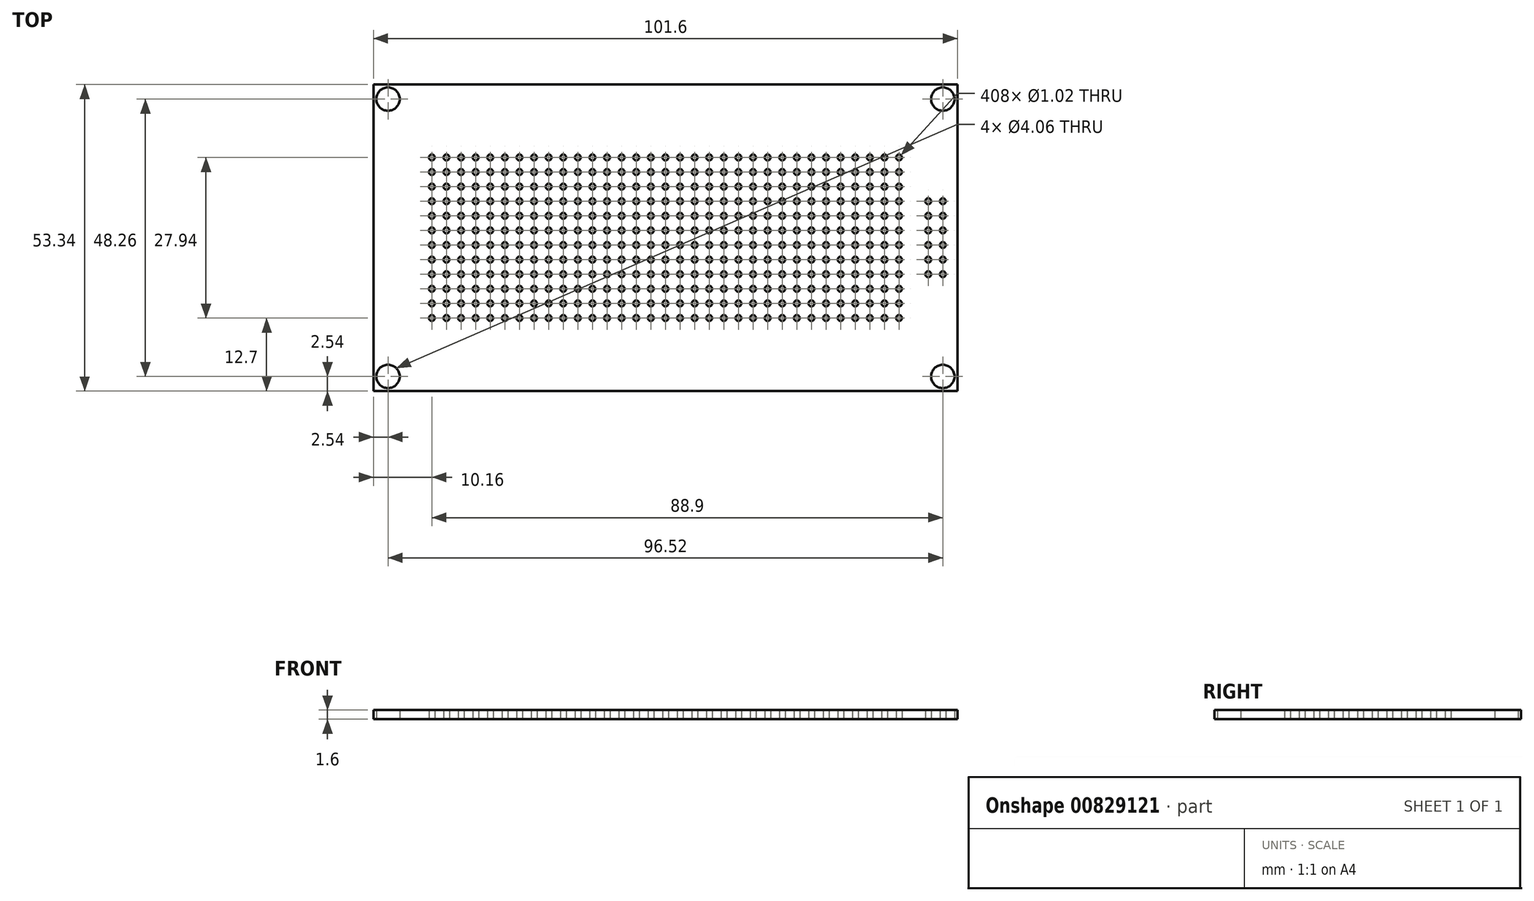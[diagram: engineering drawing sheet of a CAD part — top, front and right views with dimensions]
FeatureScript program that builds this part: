
annotation { "Feature Type Name" : "Feature", "Feature Type Description" : "" }
export const myFeature = defineFeature(function(context is Context, id is Id, definition is map)
    precondition{}
    {
        {
            var Q0;
            Q0=qCreatedBy(makeId("Top.planeOp"),FACE);
            var sketch = newSketch(context, id + "F0", { "sketchPlane" : qUnion([Q0])});
            skLineSegment(sketch, "E0.bottom", {"start": v(50.8, -26.67) * mm, "end": v(-50.8, -26.67) * mm});
            skLineSegment(sketch, "E0.top", {"start": v(50.8, 26.67) * mm, "end": v(-50.8, 26.67) * mm});
            skLineSegment(sketch, "E0.left", {"start": v(50.8, -26.67) * mm, "end": v(50.8, 26.67) * mm});
            skLineSegment(sketch, "E0.right", {"start": v(-50.8, -26.67) * mm, "end": v(-50.8, 26.67) * mm});
            skPoint(sketch, "E0.middle", {"position": v(0, 0) * mm});
            skCircle(sketch, "E1", {"center": v(-48.26, -24.13) * mm, "radius": 2.03 * mm});
            skCircle(sketch, "E2", {"center": v(-48.26, 24.13) * mm, "radius": 2.03 * mm});
            skCircle(sketch, "E3", {"center": v(48.26, 24.13) * mm, "radius": 2.03 * mm});
            skCircle(sketch, "E4", {"center": v(48.26, -24.13) * mm, "radius": 2.03 * mm});
            skCircle(sketch, "E5", {"center": v(-40.64, -13.97) * mm, "radius": 0.5 * mm});
            skCircle(sketch, "E6.0.1.0", {"center": v(-40.64, -11.43) * mm, "radius": 0.5 * mm});
            skCircle(sketch, "E6.0.2.0", {"center": v(-40.64, -8.9) * mm, "radius": 0.5 * mm});
            skCircle(sketch, "E6.0.3.0", {"center": v(-40.64, -6.35) * mm, "radius": 0.5 * mm});
            skCircle(sketch, "E6.0.4.0", {"center": v(-40.64, -3.81) * mm, "radius": 0.5 * mm});
            skCircle(sketch, "E6.0.5.0", {"center": v(-40.64, -1.27) * mm, "radius": 0.5 * mm});
            skCircle(sketch, "E6.0.6.0", {"center": v(-40.64, 1.27) * mm, "radius": 0.5 * mm});
            skCircle(sketch, "E6.0.7.0", {"center": v(-40.64, 3.8) * mm, "radius": 0.5 * mm});
            skCircle(sketch, "E6.0.8.0", {"center": v(-40.64, 6.35) * mm, "radius": 0.5 * mm});
            skCircle(sketch, "E6.0.9.0", {"center": v(-40.64, 8.89) * mm, "radius": 0.5 * mm});
            skCircle(sketch, "E6.0.10.0", {"center": v(-40.64, 11.43) * mm, "radius": 0.5 * mm});
            skCircle(sketch, "E6.0.11.0", {"center": v(-40.64, 13.97) * mm, "radius": 0.5 * mm});
            skCircle(sketch, "E6.1.0.0", {"center": v(-38.1, -13.97) * mm, "radius": 0.5 * mm});
            skCircle(sketch, "E6.1.1.0", {"center": v(-38.1, -11.43) * mm, "radius": 0.5 * mm});
            skCircle(sketch, "E6.1.2.0", {"center": v(-38.1, -8.9) * mm, "radius": 0.5 * mm});
            skCircle(sketch, "E6.1.3.0", {"center": v(-38.1, -6.35) * mm, "radius": 0.5 * mm});
            skCircle(sketch, "E6.1.4.0", {"center": v(-38.1, -3.81) * mm, "radius": 0.5 * mm});
            skCircle(sketch, "E6.1.5.0", {"center": v(-38.1, -1.27) * mm, "radius": 0.5 * mm});
            skCircle(sketch, "E6.1.6.0", {"center": v(-38.1, 1.27) * mm, "radius": 0.5 * mm});
            skCircle(sketch, "E6.1.7.0", {"center": v(-38.1, 3.8) * mm, "radius": 0.5 * mm});
            skCircle(sketch, "E6.1.8.0", {"center": v(-38.1, 6.35) * mm, "radius": 0.5 * mm});
            skCircle(sketch, "E6.1.9.0", {"center": v(-38.1, 8.89) * mm, "radius": 0.5 * mm});
            skCircle(sketch, "E6.1.10.0", {"center": v(-38.1, 11.43) * mm, "radius": 0.5 * mm});
            skCircle(sketch, "E6.1.11.0", {"center": v(-38.1, 13.97) * mm, "radius": 0.5 * mm});
            skCircle(sketch, "E6.2.0.0", {"center": v(-35.56, -13.97) * mm, "radius": 0.5 * mm});
            skCircle(sketch, "E6.2.1.0", {"center": v(-35.56, -11.43) * mm, "radius": 0.5 * mm});
            skCircle(sketch, "E6.2.2.0", {"center": v(-35.56, -8.9) * mm, "radius": 0.5 * mm});
            skCircle(sketch, "E6.2.3.0", {"center": v(-35.56, -6.35) * mm, "radius": 0.5 * mm});
            skCircle(sketch, "E6.2.4.0", {"center": v(-35.56, -3.81) * mm, "radius": 0.5 * mm});
            skCircle(sketch, "E6.2.5.0", {"center": v(-35.56, -1.27) * mm, "radius": 0.5 * mm});
            skCircle(sketch, "E6.2.6.0", {"center": v(-35.56, 1.27) * mm, "radius": 0.5 * mm});
            skCircle(sketch, "E6.2.7.0", {"center": v(-35.56, 3.8) * mm, "radius": 0.5 * mm});
            skCircle(sketch, "E6.2.8.0", {"center": v(-35.56, 6.35) * mm, "radius": 0.5 * mm});
            skCircle(sketch, "E6.2.9.0", {"center": v(-35.56, 8.89) * mm, "radius": 0.5 * mm});
            skCircle(sketch, "E6.2.10.0", {"center": v(-35.56, 11.43) * mm, "radius": 0.5 * mm});
            skCircle(sketch, "E6.2.11.0", {"center": v(-35.56, 13.97) * mm, "radius": 0.5 * mm});
            skCircle(sketch, "E6.3.0.0", {"center": v(-33.02, -13.97) * mm, "radius": 0.5 * mm});
            skCircle(sketch, "E6.3.1.0", {"center": v(-33.02, -11.43) * mm, "radius": 0.5 * mm});
            skCircle(sketch, "E6.3.2.0", {"center": v(-33.02, -8.9) * mm, "radius": 0.5 * mm});
            skCircle(sketch, "E6.3.3.0", {"center": v(-33.02, -6.35) * mm, "radius": 0.5 * mm});
            skCircle(sketch, "E6.3.4.0", {"center": v(-33.02, -3.81) * mm, "radius": 0.5 * mm});
            skCircle(sketch, "E6.3.5.0", {"center": v(-33.02, -1.27) * mm, "radius": 0.5 * mm});
            skCircle(sketch, "E6.3.6.0", {"center": v(-33.02, 1.27) * mm, "radius": 0.5 * mm});
            skCircle(sketch, "E6.3.7.0", {"center": v(-33.02, 3.8) * mm, "radius": 0.5 * mm});
            skCircle(sketch, "E6.3.8.0", {"center": v(-33.02, 6.35) * mm, "radius": 0.5 * mm});
            skCircle(sketch, "E6.3.9.0", {"center": v(-33.02, 8.89) * mm, "radius": 0.5 * mm});
            skCircle(sketch, "E6.3.10.0", {"center": v(-33.02, 11.43) * mm, "radius": 0.5 * mm});
            skCircle(sketch, "E6.3.11.0", {"center": v(-33.02, 13.97) * mm, "radius": 0.5 * mm});
            skCircle(sketch, "E6.4.0.0", {"center": v(-30.48, -13.97) * mm, "radius": 0.5 * mm});
            skCircle(sketch, "E6.4.1.0", {"center": v(-30.48, -11.43) * mm, "radius": 0.5 * mm});
            skCircle(sketch, "E6.4.2.0", {"center": v(-30.48, -8.9) * mm, "radius": 0.5 * mm});
            skCircle(sketch, "E6.4.3.0", {"center": v(-30.48, -6.35) * mm, "radius": 0.5 * mm});
            skCircle(sketch, "E6.4.4.0", {"center": v(-30.48, -3.81) * mm, "radius": 0.5 * mm});
            skCircle(sketch, "E6.4.5.0", {"center": v(-30.48, -1.27) * mm, "radius": 0.5 * mm});
            skCircle(sketch, "E6.4.6.0", {"center": v(-30.48, 1.27) * mm, "radius": 0.5 * mm});
            skCircle(sketch, "E6.4.7.0", {"center": v(-30.48, 3.8) * mm, "radius": 0.5 * mm});
            skCircle(sketch, "E6.4.8.0", {"center": v(-30.48, 6.35) * mm, "radius": 0.5 * mm});
            skCircle(sketch, "E6.4.9.0", {"center": v(-30.48, 8.89) * mm, "radius": 0.5 * mm});
            skCircle(sketch, "E6.4.10.0", {"center": v(-30.48, 11.43) * mm, "radius": 0.5 * mm});
            skCircle(sketch, "E6.4.11.0", {"center": v(-30.48, 13.97) * mm, "radius": 0.5 * mm});
            skCircle(sketch, "E6.5.0.0", {"center": v(-27.94, -13.97) * mm, "radius": 0.5 * mm});
            skCircle(sketch, "E6.5.1.0", {"center": v(-27.94, -11.43) * mm, "radius": 0.5 * mm});
            skCircle(sketch, "E6.5.2.0", {"center": v(-27.94, -8.9) * mm, "radius": 0.5 * mm});
            skCircle(sketch, "E6.5.3.0", {"center": v(-27.94, -6.35) * mm, "radius": 0.5 * mm});
            skCircle(sketch, "E6.5.4.0", {"center": v(-27.94, -3.81) * mm, "radius": 0.5 * mm});
            skCircle(sketch, "E6.5.5.0", {"center": v(-27.94, -1.27) * mm, "radius": 0.5 * mm});
            skCircle(sketch, "E6.5.6.0", {"center": v(-27.94, 1.27) * mm, "radius": 0.5 * mm});
            skCircle(sketch, "E6.5.7.0", {"center": v(-27.94, 3.8) * mm, "radius": 0.5 * mm});
            skCircle(sketch, "E6.5.8.0", {"center": v(-27.94, 6.35) * mm, "radius": 0.5 * mm});
            skCircle(sketch, "E6.5.9.0", {"center": v(-27.94, 8.89) * mm, "radius": 0.5 * mm});
            skCircle(sketch, "E6.5.10.0", {"center": v(-27.94, 11.43) * mm, "radius": 0.5 * mm});
            skCircle(sketch, "E6.5.11.0", {"center": v(-27.94, 13.97) * mm, "radius": 0.5 * mm});
            skCircle(sketch, "E6.6.0.0", {"center": v(-25.4, -13.97) * mm, "radius": 0.5 * mm});
            skCircle(sketch, "E6.6.1.0", {"center": v(-25.4, -11.43) * mm, "radius": 0.5 * mm});
            skCircle(sketch, "E6.6.2.0", {"center": v(-25.4, -8.9) * mm, "radius": 0.5 * mm});
            skCircle(sketch, "E6.6.3.0", {"center": v(-25.4, -6.35) * mm, "radius": 0.5 * mm});
            skCircle(sketch, "E6.6.4.0", {"center": v(-25.4, -3.81) * mm, "radius": 0.5 * mm});
            skCircle(sketch, "E6.6.5.0", {"center": v(-25.4, -1.27) * mm, "radius": 0.5 * mm});
            skCircle(sketch, "E6.6.6.0", {"center": v(-25.4, 1.27) * mm, "radius": 0.5 * mm});
            skCircle(sketch, "E6.6.7.0", {"center": v(-25.4, 3.8) * mm, "radius": 0.5 * mm});
            skCircle(sketch, "E6.6.8.0", {"center": v(-25.4, 6.35) * mm, "radius": 0.5 * mm});
            skCircle(sketch, "E6.6.9.0", {"center": v(-25.4, 8.89) * mm, "radius": 0.5 * mm});
            skCircle(sketch, "E6.6.10.0", {"center": v(-25.4, 11.43) * mm, "radius": 0.5 * mm});
            skCircle(sketch, "E6.6.11.0", {"center": v(-25.4, 13.97) * mm, "radius": 0.5 * mm});
            skCircle(sketch, "E6.7.0.0", {"center": v(-22.86, -13.97) * mm, "radius": 0.5 * mm});
            skCircle(sketch, "E6.7.1.0", {"center": v(-22.86, -11.43) * mm, "radius": 0.5 * mm});
            skCircle(sketch, "E6.7.2.0", {"center": v(-22.86, -8.9) * mm, "radius": 0.5 * mm});
            skCircle(sketch, "E6.7.3.0", {"center": v(-22.86, -6.35) * mm, "radius": 0.5 * mm});
            skCircle(sketch, "E6.7.4.0", {"center": v(-22.86, -3.81) * mm, "radius": 0.5 * mm});
            skCircle(sketch, "E6.7.5.0", {"center": v(-22.86, -1.27) * mm, "radius": 0.5 * mm});
            skCircle(sketch, "E6.7.6.0", {"center": v(-22.86, 1.27) * mm, "radius": 0.5 * mm});
            skCircle(sketch, "E6.7.7.0", {"center": v(-22.86, 3.8) * mm, "radius": 0.5 * mm});
            skCircle(sketch, "E6.7.8.0", {"center": v(-22.86, 6.35) * mm, "radius": 0.5 * mm});
            skCircle(sketch, "E6.7.9.0", {"center": v(-22.86, 8.89) * mm, "radius": 0.5 * mm});
            skCircle(sketch, "E6.7.10.0", {"center": v(-22.86, 11.43) * mm, "radius": 0.5 * mm});
            skCircle(sketch, "E6.7.11.0", {"center": v(-22.86, 13.97) * mm, "radius": 0.5 * mm});
            skCircle(sketch, "E6.8.0.0", {"center": v(-20.32, -13.97) * mm, "radius": 0.5 * mm});
            skCircle(sketch, "E6.8.1.0", {"center": v(-20.32, -11.43) * mm, "radius": 0.5 * mm});
            skCircle(sketch, "E6.8.2.0", {"center": v(-20.32, -8.9) * mm, "radius": 0.5 * mm});
            skCircle(sketch, "E6.8.3.0", {"center": v(-20.32, -6.35) * mm, "radius": 0.5 * mm});
            skCircle(sketch, "E6.8.4.0", {"center": v(-20.32, -3.81) * mm, "radius": 0.5 * mm});
            skCircle(sketch, "E6.8.5.0", {"center": v(-20.32, -1.27) * mm, "radius": 0.5 * mm});
            skCircle(sketch, "E6.8.6.0", {"center": v(-20.32, 1.27) * mm, "radius": 0.5 * mm});
            skCircle(sketch, "E6.8.7.0", {"center": v(-20.32, 3.8) * mm, "radius": 0.5 * mm});
            skCircle(sketch, "E6.8.8.0", {"center": v(-20.32, 6.35) * mm, "radius": 0.5 * mm});
            skCircle(sketch, "E6.8.9.0", {"center": v(-20.32, 8.89) * mm, "radius": 0.5 * mm});
            skCircle(sketch, "E6.8.10.0", {"center": v(-20.32, 11.43) * mm, "radius": 0.5 * mm});
            skCircle(sketch, "E6.8.11.0", {"center": v(-20.32, 13.97) * mm, "radius": 0.5 * mm});
            skCircle(sketch, "E6.9.0.0", {"center": v(-17.78, -13.97) * mm, "radius": 0.5 * mm});
            skCircle(sketch, "E6.9.1.0", {"center": v(-17.78, -11.43) * mm, "radius": 0.5 * mm});
            skCircle(sketch, "E6.9.2.0", {"center": v(-17.78, -8.9) * mm, "radius": 0.5 * mm});
            skCircle(sketch, "E6.9.3.0", {"center": v(-17.78, -6.35) * mm, "radius": 0.5 * mm});
            skCircle(sketch, "E6.9.4.0", {"center": v(-17.78, -3.81) * mm, "radius": 0.5 * mm});
            skCircle(sketch, "E6.9.5.0", {"center": v(-17.78, -1.27) * mm, "radius": 0.5 * mm});
            skCircle(sketch, "E6.9.6.0", {"center": v(-17.78, 1.27) * mm, "radius": 0.5 * mm});
            skCircle(sketch, "E6.9.7.0", {"center": v(-17.78, 3.8) * mm, "radius": 0.5 * mm});
            skCircle(sketch, "E6.9.8.0", {"center": v(-17.78, 6.35) * mm, "radius": 0.5 * mm});
            skCircle(sketch, "E6.9.9.0", {"center": v(-17.78, 8.89) * mm, "radius": 0.5 * mm});
            skCircle(sketch, "E6.9.10.0", {"center": v(-17.78, 11.43) * mm, "radius": 0.5 * mm});
            skCircle(sketch, "E6.9.11.0", {"center": v(-17.78, 13.97) * mm, "radius": 0.5 * mm});
            skCircle(sketch, "E6.10.0.0", {"center": v(-15.24, -13.97) * mm, "radius": 0.5 * mm});
            skCircle(sketch, "E6.10.1.0", {"center": v(-15.24, -11.43) * mm, "radius": 0.5 * mm});
            skCircle(sketch, "E6.10.2.0", {"center": v(-15.24, -8.9) * mm, "radius": 0.5 * mm});
            skCircle(sketch, "E6.10.3.0", {"center": v(-15.24, -6.35) * mm, "radius": 0.5 * mm});
            skCircle(sketch, "E6.10.4.0", {"center": v(-15.24, -3.81) * mm, "radius": 0.5 * mm});
            skCircle(sketch, "E6.10.5.0", {"center": v(-15.24, -1.27) * mm, "radius": 0.5 * mm});
            skCircle(sketch, "E6.10.6.0", {"center": v(-15.24, 1.27) * mm, "radius": 0.5 * mm});
            skCircle(sketch, "E6.10.7.0", {"center": v(-15.24, 3.8) * mm, "radius": 0.5 * mm});
            skCircle(sketch, "E6.10.8.0", {"center": v(-15.24, 6.35) * mm, "radius": 0.5 * mm});
            skCircle(sketch, "E6.10.9.0", {"center": v(-15.24, 8.89) * mm, "radius": 0.5 * mm});
            skCircle(sketch, "E6.10.10.0", {"center": v(-15.24, 11.43) * mm, "radius": 0.5 * mm});
            skCircle(sketch, "E6.10.11.0", {"center": v(-15.24, 13.97) * mm, "radius": 0.5 * mm});
            skCircle(sketch, "E6.11.0.0", {"center": v(-12.7, -13.97) * mm, "radius": 0.5 * mm});
            skCircle(sketch, "E6.11.1.0", {"center": v(-12.7, -11.43) * mm, "radius": 0.5 * mm});
            skCircle(sketch, "E6.11.2.0", {"center": v(-12.7, -8.9) * mm, "radius": 0.5 * mm});
            skCircle(sketch, "E6.11.3.0", {"center": v(-12.7, -6.35) * mm, "radius": 0.5 * mm});
            skCircle(sketch, "E6.11.4.0", {"center": v(-12.7, -3.81) * mm, "radius": 0.5 * mm});
            skCircle(sketch, "E6.11.5.0", {"center": v(-12.7, -1.27) * mm, "radius": 0.5 * mm});
            skCircle(sketch, "E6.11.6.0", {"center": v(-12.7, 1.27) * mm, "radius": 0.5 * mm});
            skCircle(sketch, "E6.11.7.0", {"center": v(-12.7, 3.8) * mm, "radius": 0.5 * mm});
            skCircle(sketch, "E6.11.8.0", {"center": v(-12.7, 6.35) * mm, "radius": 0.5 * mm});
            skCircle(sketch, "E6.11.9.0", {"center": v(-12.7, 8.89) * mm, "radius": 0.5 * mm});
            skCircle(sketch, "E6.11.10.0", {"center": v(-12.7, 11.43) * mm, "radius": 0.5 * mm});
            skCircle(sketch, "E6.11.11.0", {"center": v(-12.7, 13.97) * mm, "radius": 0.5 * mm});
            skCircle(sketch, "E6.12.0.0", {"center": v(-10.16, -13.97) * mm, "radius": 0.5 * mm});
            skCircle(sketch, "E6.12.1.0", {"center": v(-10.16, -11.43) * mm, "radius": 0.5 * mm});
            skCircle(sketch, "E6.12.2.0", {"center": v(-10.16, -8.9) * mm, "radius": 0.5 * mm});
            skCircle(sketch, "E6.12.3.0", {"center": v(-10.16, -6.35) * mm, "radius": 0.5 * mm});
            skCircle(sketch, "E6.12.4.0", {"center": v(-10.16, -3.81) * mm, "radius": 0.5 * mm});
            skCircle(sketch, "E6.12.5.0", {"center": v(-10.16, -1.27) * mm, "radius": 0.5 * mm});
            skCircle(sketch, "E6.12.6.0", {"center": v(-10.16, 1.27) * mm, "radius": 0.5 * mm});
            skCircle(sketch, "E6.12.7.0", {"center": v(-10.16, 3.8) * mm, "radius": 0.5 * mm});
            skCircle(sketch, "E6.12.8.0", {"center": v(-10.16, 6.35) * mm, "radius": 0.5 * mm});
            skCircle(sketch, "E6.12.9.0", {"center": v(-10.16, 8.89) * mm, "radius": 0.5 * mm});
            skCircle(sketch, "E6.12.10.0", {"center": v(-10.16, 11.43) * mm, "radius": 0.5 * mm});
            skCircle(sketch, "E6.12.11.0", {"center": v(-10.16, 13.97) * mm, "radius": 0.5 * mm});
            skCircle(sketch, "E6.13.0.0", {"center": v(-7.62, -13.97) * mm, "radius": 0.5 * mm});
            skCircle(sketch, "E6.13.1.0", {"center": v(-7.62, -11.43) * mm, "radius": 0.5 * mm});
            skCircle(sketch, "E6.13.2.0", {"center": v(-7.62, -8.9) * mm, "radius": 0.5 * mm});
            skCircle(sketch, "E6.13.3.0", {"center": v(-7.62, -6.35) * mm, "radius": 0.5 * mm});
            skCircle(sketch, "E6.13.4.0", {"center": v(-7.62, -3.81) * mm, "radius": 0.5 * mm});
            skCircle(sketch, "E6.13.5.0", {"center": v(-7.62, -1.27) * mm, "radius": 0.5 * mm});
            skCircle(sketch, "E6.13.6.0", {"center": v(-7.62, 1.27) * mm, "radius": 0.5 * mm});
            skCircle(sketch, "E6.13.7.0", {"center": v(-7.62, 3.8) * mm, "radius": 0.5 * mm});
            skCircle(sketch, "E6.13.8.0", {"center": v(-7.62, 6.35) * mm, "radius": 0.5 * mm});
            skCircle(sketch, "E6.13.9.0", {"center": v(-7.62, 8.89) * mm, "radius": 0.5 * mm});
            skCircle(sketch, "E6.13.10.0", {"center": v(-7.62, 11.43) * mm, "radius": 0.5 * mm});
            skCircle(sketch, "E6.13.11.0", {"center": v(-7.62, 13.97) * mm, "radius": 0.5 * mm});
            skCircle(sketch, "E6.14.0.0", {"center": v(-5.08, -13.97) * mm, "radius": 0.5 * mm});
            skCircle(sketch, "E6.14.1.0", {"center": v(-5.08, -11.43) * mm, "radius": 0.5 * mm});
            skCircle(sketch, "E6.14.2.0", {"center": v(-5.08, -8.9) * mm, "radius": 0.5 * mm});
            skCircle(sketch, "E6.14.3.0", {"center": v(-5.08, -6.35) * mm, "radius": 0.5 * mm});
            skCircle(sketch, "E6.14.4.0", {"center": v(-5.08, -3.81) * mm, "radius": 0.5 * mm});
            skCircle(sketch, "E6.14.5.0", {"center": v(-5.08, -1.27) * mm, "radius": 0.5 * mm});
            skCircle(sketch, "E6.14.6.0", {"center": v(-5.08, 1.27) * mm, "radius": 0.5 * mm});
            skCircle(sketch, "E6.14.7.0", {"center": v(-5.08, 3.8) * mm, "radius": 0.5 * mm});
            skCircle(sketch, "E6.14.8.0", {"center": v(-5.08, 6.35) * mm, "radius": 0.5 * mm});
            skCircle(sketch, "E6.14.9.0", {"center": v(-5.08, 8.89) * mm, "radius": 0.5 * mm});
            skCircle(sketch, "E6.14.10.0", {"center": v(-5.08, 11.43) * mm, "radius": 0.5 * mm});
            skCircle(sketch, "E6.14.11.0", {"center": v(-5.08, 13.97) * mm, "radius": 0.5 * mm});
            skCircle(sketch, "E6.15.0.0", {"center": v(-2.54, -13.97) * mm, "radius": 0.5 * mm});
            skCircle(sketch, "E6.15.1.0", {"center": v(-2.54, -11.43) * mm, "radius": 0.5 * mm});
            skCircle(sketch, "E6.15.2.0", {"center": v(-2.54, -8.9) * mm, "radius": 0.5 * mm});
            skCircle(sketch, "E6.15.3.0", {"center": v(-2.54, -6.35) * mm, "radius": 0.5 * mm});
            skCircle(sketch, "E6.15.4.0", {"center": v(-2.54, -3.81) * mm, "radius": 0.5 * mm});
            skCircle(sketch, "E6.15.5.0", {"center": v(-2.54, -1.27) * mm, "radius": 0.5 * mm});
            skCircle(sketch, "E6.15.6.0", {"center": v(-2.54, 1.27) * mm, "radius": 0.5 * mm});
            skCircle(sketch, "E6.15.7.0", {"center": v(-2.54, 3.8) * mm, "radius": 0.5 * mm});
            skCircle(sketch, "E6.15.8.0", {"center": v(-2.54, 6.35) * mm, "radius": 0.5 * mm});
            skCircle(sketch, "E6.15.9.0", {"center": v(-2.54, 8.89) * mm, "radius": 0.5 * mm});
            skCircle(sketch, "E6.15.10.0", {"center": v(-2.54, 11.43) * mm, "radius": 0.5 * mm});
            skCircle(sketch, "E6.15.11.0", {"center": v(-2.54, 13.97) * mm, "radius": 0.5 * mm});
            skCircle(sketch, "E6.16.0.0", {"center": v(0, -13.97) * mm, "radius": 0.5 * mm});
            skCircle(sketch, "E6.16.1.0", {"center": v(0, -11.43) * mm, "radius": 0.5 * mm});
            skCircle(sketch, "E6.16.2.0", {"center": v(0, -8.9) * mm, "radius": 0.5 * mm});
            skCircle(sketch, "E6.16.3.0", {"center": v(0, -6.35) * mm, "radius": 0.5 * mm});
            skCircle(sketch, "E6.16.4.0", {"center": v(0, -3.81) * mm, "radius": 0.5 * mm});
            skCircle(sketch, "E6.16.5.0", {"center": v(0, -1.27) * mm, "radius": 0.5 * mm});
            skCircle(sketch, "E6.16.6.0", {"center": v(0, 1.27) * mm, "radius": 0.5 * mm});
            skCircle(sketch, "E6.16.7.0", {"center": v(0, 3.8) * mm, "radius": 0.5 * mm});
            skCircle(sketch, "E6.16.8.0", {"center": v(0, 6.35) * mm, "radius": 0.5 * mm});
            skCircle(sketch, "E6.16.9.0", {"center": v(0, 8.89) * mm, "radius": 0.5 * mm});
            skCircle(sketch, "E6.16.10.0", {"center": v(0, 11.43) * mm, "radius": 0.5 * mm});
            skCircle(sketch, "E6.16.11.0", {"center": v(0, 13.97) * mm, "radius": 0.5 * mm});
            skCircle(sketch, "E6.17.0.0", {"center": v(2.54, -13.97) * mm, "radius": 0.5 * mm});
            skCircle(sketch, "E6.17.1.0", {"center": v(2.54, -11.43) * mm, "radius": 0.5 * mm});
            skCircle(sketch, "E6.17.2.0", {"center": v(2.54, -8.9) * mm, "radius": 0.5 * mm});
            skCircle(sketch, "E6.17.3.0", {"center": v(2.54, -6.35) * mm, "radius": 0.5 * mm});
            skCircle(sketch, "E6.17.4.0", {"center": v(2.54, -3.81) * mm, "radius": 0.5 * mm});
            skCircle(sketch, "E6.17.5.0", {"center": v(2.54, -1.27) * mm, "radius": 0.5 * mm});
            skCircle(sketch, "E6.17.6.0", {"center": v(2.54, 1.27) * mm, "radius": 0.5 * mm});
            skCircle(sketch, "E6.17.7.0", {"center": v(2.54, 3.8) * mm, "radius": 0.5 * mm});
            skCircle(sketch, "E6.17.8.0", {"center": v(2.54, 6.35) * mm, "radius": 0.5 * mm});
            skCircle(sketch, "E6.17.9.0", {"center": v(2.54, 8.89) * mm, "radius": 0.5 * mm});
            skCircle(sketch, "E6.17.10.0", {"center": v(2.54, 11.43) * mm, "radius": 0.5 * mm});
            skCircle(sketch, "E6.17.11.0", {"center": v(2.54, 13.97) * mm, "radius": 0.5 * mm});
            skCircle(sketch, "E6.18.0.0", {"center": v(5.08, -13.97) * mm, "radius": 0.5 * mm});
            skCircle(sketch, "E6.18.1.0", {"center": v(5.08, -11.43) * mm, "radius": 0.5 * mm});
            skCircle(sketch, "E6.18.2.0", {"center": v(5.08, -8.9) * mm, "radius": 0.5 * mm});
            skCircle(sketch, "E6.18.3.0", {"center": v(5.08, -6.35) * mm, "radius": 0.5 * mm});
            skCircle(sketch, "E6.18.4.0", {"center": v(5.08, -3.81) * mm, "radius": 0.5 * mm});
            skCircle(sketch, "E6.18.5.0", {"center": v(5.08, -1.27) * mm, "radius": 0.5 * mm});
            skCircle(sketch, "E6.18.6.0", {"center": v(5.08, 1.27) * mm, "radius": 0.5 * mm});
            skCircle(sketch, "E6.18.7.0", {"center": v(5.08, 3.8) * mm, "radius": 0.5 * mm});
            skCircle(sketch, "E6.18.8.0", {"center": v(5.08, 6.35) * mm, "radius": 0.5 * mm});
            skCircle(sketch, "E6.18.9.0", {"center": v(5.08, 8.89) * mm, "radius": 0.5 * mm});
            skCircle(sketch, "E6.18.10.0", {"center": v(5.08, 11.43) * mm, "radius": 0.5 * mm});
            skCircle(sketch, "E6.18.11.0", {"center": v(5.08, 13.97) * mm, "radius": 0.5 * mm});
            skCircle(sketch, "E6.19.0.0", {"center": v(7.62, -13.97) * mm, "radius": 0.5 * mm});
            skCircle(sketch, "E6.19.1.0", {"center": v(7.62, -11.43) * mm, "radius": 0.5 * mm});
            skCircle(sketch, "E6.19.2.0", {"center": v(7.62, -8.9) * mm, "radius": 0.5 * mm});
            skCircle(sketch, "E6.19.3.0", {"center": v(7.62, -6.35) * mm, "radius": 0.5 * mm});
            skCircle(sketch, "E6.19.4.0", {"center": v(7.62, -3.81) * mm, "radius": 0.5 * mm});
            skCircle(sketch, "E6.19.5.0", {"center": v(7.62, -1.27) * mm, "radius": 0.5 * mm});
            skCircle(sketch, "E6.19.6.0", {"center": v(7.62, 1.27) * mm, "radius": 0.5 * mm});
            skCircle(sketch, "E6.19.7.0", {"center": v(7.62, 3.8) * mm, "radius": 0.5 * mm});
            skCircle(sketch, "E6.19.8.0", {"center": v(7.62, 6.35) * mm, "radius": 0.5 * mm});
            skCircle(sketch, "E6.19.9.0", {"center": v(7.62, 8.89) * mm, "radius": 0.5 * mm});
            skCircle(sketch, "E6.19.10.0", {"center": v(7.62, 11.43) * mm, "radius": 0.5 * mm});
            skCircle(sketch, "E6.19.11.0", {"center": v(7.62, 13.97) * mm, "radius": 0.5 * mm});
            skCircle(sketch, "E6.20.0.0", {"center": v(10.16, -13.97) * mm, "radius": 0.5 * mm});
            skCircle(sketch, "E6.20.1.0", {"center": v(10.16, -11.43) * mm, "radius": 0.5 * mm});
            skCircle(sketch, "E6.20.2.0", {"center": v(10.16, -8.9) * mm, "radius": 0.5 * mm});
            skCircle(sketch, "E6.20.3.0", {"center": v(10.16, -6.35) * mm, "radius": 0.5 * mm});
            skCircle(sketch, "E6.20.4.0", {"center": v(10.16, -3.81) * mm, "radius": 0.5 * mm});
            skCircle(sketch, "E6.20.5.0", {"center": v(10.16, -1.27) * mm, "radius": 0.5 * mm});
            skCircle(sketch, "E6.20.6.0", {"center": v(10.16, 1.27) * mm, "radius": 0.5 * mm});
            skCircle(sketch, "E6.20.7.0", {"center": v(10.16, 3.8) * mm, "radius": 0.5 * mm});
            skCircle(sketch, "E6.20.8.0", {"center": v(10.16, 6.35) * mm, "radius": 0.5 * mm});
            skCircle(sketch, "E6.20.9.0", {"center": v(10.16, 8.89) * mm, "radius": 0.5 * mm});
            skCircle(sketch, "E6.20.10.0", {"center": v(10.16, 11.43) * mm, "radius": 0.5 * mm});
            skCircle(sketch, "E6.20.11.0", {"center": v(10.16, 13.97) * mm, "radius": 0.5 * mm});
            skCircle(sketch, "E6.21.0.0", {"center": v(12.7, -13.97) * mm, "radius": 0.5 * mm});
            skCircle(sketch, "E6.21.1.0", {"center": v(12.7, -11.43) * mm, "radius": 0.5 * mm});
            skCircle(sketch, "E6.21.2.0", {"center": v(12.7, -8.9) * mm, "radius": 0.5 * mm});
            skCircle(sketch, "E6.21.3.0", {"center": v(12.7, -6.35) * mm, "radius": 0.5 * mm});
            skCircle(sketch, "E6.21.4.0", {"center": v(12.7, -3.81) * mm, "radius": 0.5 * mm});
            skCircle(sketch, "E6.21.5.0", {"center": v(12.7, -1.27) * mm, "radius": 0.5 * mm});
            skCircle(sketch, "E6.21.6.0", {"center": v(12.7, 1.27) * mm, "radius": 0.5 * mm});
            skCircle(sketch, "E6.21.7.0", {"center": v(12.7, 3.8) * mm, "radius": 0.5 * mm});
            skCircle(sketch, "E6.21.8.0", {"center": v(12.7, 6.35) * mm, "radius": 0.5 * mm});
            skCircle(sketch, "E6.21.9.0", {"center": v(12.7, 8.89) * mm, "radius": 0.5 * mm});
            skCircle(sketch, "E6.21.10.0", {"center": v(12.7, 11.43) * mm, "radius": 0.5 * mm});
            skCircle(sketch, "E6.21.11.0", {"center": v(12.7, 13.97) * mm, "radius": 0.5 * mm});
            skCircle(sketch, "E6.22.0.0", {"center": v(15.24, -13.97) * mm, "radius": 0.5 * mm});
            skCircle(sketch, "E6.22.1.0", {"center": v(15.24, -11.43) * mm, "radius": 0.5 * mm});
            skCircle(sketch, "E6.22.2.0", {"center": v(15.24, -8.9) * mm, "radius": 0.5 * mm});
            skCircle(sketch, "E6.22.3.0", {"center": v(15.24, -6.35) * mm, "radius": 0.5 * mm});
            skCircle(sketch, "E6.22.4.0", {"center": v(15.24, -3.81) * mm, "radius": 0.5 * mm});
            skCircle(sketch, "E6.22.5.0", {"center": v(15.24, -1.27) * mm, "radius": 0.5 * mm});
            skCircle(sketch, "E6.22.6.0", {"center": v(15.24, 1.27) * mm, "radius": 0.5 * mm});
            skCircle(sketch, "E6.22.7.0", {"center": v(15.24, 3.8) * mm, "radius": 0.5 * mm});
            skCircle(sketch, "E6.22.8.0", {"center": v(15.24, 6.35) * mm, "radius": 0.5 * mm});
            skCircle(sketch, "E6.22.9.0", {"center": v(15.24, 8.89) * mm, "radius": 0.5 * mm});
            skCircle(sketch, "E6.22.10.0", {"center": v(15.24, 11.43) * mm, "radius": 0.5 * mm});
            skCircle(sketch, "E6.22.11.0", {"center": v(15.24, 13.97) * mm, "radius": 0.5 * mm});
            skCircle(sketch, "E6.23.0.0", {"center": v(17.78, -13.97) * mm, "radius": 0.5 * mm});
            skCircle(sketch, "E6.23.1.0", {"center": v(17.78, -11.43) * mm, "radius": 0.5 * mm});
            skCircle(sketch, "E6.23.2.0", {"center": v(17.78, -8.9) * mm, "radius": 0.5 * mm});
            skCircle(sketch, "E6.23.3.0", {"center": v(17.78, -6.35) * mm, "radius": 0.5 * mm});
            skCircle(sketch, "E6.23.4.0", {"center": v(17.78, -3.81) * mm, "radius": 0.5 * mm});
            skCircle(sketch, "E6.23.5.0", {"center": v(17.78, -1.27) * mm, "radius": 0.5 * mm});
            skCircle(sketch, "E6.23.6.0", {"center": v(17.78, 1.27) * mm, "radius": 0.5 * mm});
            skCircle(sketch, "E6.23.7.0", {"center": v(17.78, 3.8) * mm, "radius": 0.5 * mm});
            skCircle(sketch, "E6.23.8.0", {"center": v(17.78, 6.35) * mm, "radius": 0.5 * mm});
            skCircle(sketch, "E6.23.9.0", {"center": v(17.78, 8.89) * mm, "radius": 0.5 * mm});
            skCircle(sketch, "E6.23.10.0", {"center": v(17.78, 11.43) * mm, "radius": 0.5 * mm});
            skCircle(sketch, "E6.23.11.0", {"center": v(17.78, 13.97) * mm, "radius": 0.5 * mm});
            skCircle(sketch, "E6.24.0.0", {"center": v(20.32, -13.97) * mm, "radius": 0.5 * mm});
            skCircle(sketch, "E6.24.1.0", {"center": v(20.32, -11.43) * mm, "radius": 0.5 * mm});
            skCircle(sketch, "E6.24.2.0", {"center": v(20.32, -8.9) * mm, "radius": 0.5 * mm});
            skCircle(sketch, "E6.24.3.0", {"center": v(20.32, -6.35) * mm, "radius": 0.5 * mm});
            skCircle(sketch, "E6.24.4.0", {"center": v(20.32, -3.81) * mm, "radius": 0.5 * mm});
            skCircle(sketch, "E6.24.5.0", {"center": v(20.32, -1.27) * mm, "radius": 0.5 * mm});
            skCircle(sketch, "E6.24.6.0", {"center": v(20.32, 1.27) * mm, "radius": 0.5 * mm});
            skCircle(sketch, "E6.24.7.0", {"center": v(20.32, 3.8) * mm, "radius": 0.5 * mm});
            skCircle(sketch, "E6.24.8.0", {"center": v(20.32, 6.35) * mm, "radius": 0.5 * mm});
            skCircle(sketch, "E6.24.9.0", {"center": v(20.32, 8.89) * mm, "radius": 0.5 * mm});
            skCircle(sketch, "E6.24.10.0", {"center": v(20.32, 11.43) * mm, "radius": 0.5 * mm});
            skCircle(sketch, "E6.24.11.0", {"center": v(20.32, 13.97) * mm, "radius": 0.5 * mm});
            skCircle(sketch, "E6.25.0.0", {"center": v(22.86, -13.97) * mm, "radius": 0.5 * mm});
            skCircle(sketch, "E6.25.1.0", {"center": v(22.86, -11.43) * mm, "radius": 0.5 * mm});
            skCircle(sketch, "E6.25.2.0", {"center": v(22.86, -8.9) * mm, "radius": 0.5 * mm});
            skCircle(sketch, "E6.25.3.0", {"center": v(22.86, -6.35) * mm, "radius": 0.5 * mm});
            skCircle(sketch, "E6.25.4.0", {"center": v(22.86, -3.81) * mm, "radius": 0.5 * mm});
            skCircle(sketch, "E6.25.5.0", {"center": v(22.86, -1.27) * mm, "radius": 0.5 * mm});
            skCircle(sketch, "E6.25.6.0", {"center": v(22.86, 1.27) * mm, "radius": 0.5 * mm});
            skCircle(sketch, "E6.25.7.0", {"center": v(22.86, 3.8) * mm, "radius": 0.5 * mm});
            skCircle(sketch, "E6.25.8.0", {"center": v(22.86, 6.35) * mm, "radius": 0.5 * mm});
            skCircle(sketch, "E6.25.9.0", {"center": v(22.86, 8.89) * mm, "radius": 0.5 * mm});
            skCircle(sketch, "E6.25.10.0", {"center": v(22.86, 11.43) * mm, "radius": 0.5 * mm});
            skCircle(sketch, "E6.25.11.0", {"center": v(22.86, 13.97) * mm, "radius": 0.5 * mm});
            skCircle(sketch, "E6.26.0.0", {"center": v(25.4, -13.97) * mm, "radius": 0.5 * mm});
            skCircle(sketch, "E6.26.1.0", {"center": v(25.4, -11.43) * mm, "radius": 0.5 * mm});
            skCircle(sketch, "E6.26.2.0", {"center": v(25.4, -8.9) * mm, "radius": 0.5 * mm});
            skCircle(sketch, "E6.26.3.0", {"center": v(25.4, -6.35) * mm, "radius": 0.5 * mm});
            skCircle(sketch, "E6.26.4.0", {"center": v(25.4, -3.81) * mm, "radius": 0.5 * mm});
            skCircle(sketch, "E6.26.5.0", {"center": v(25.4, -1.27) * mm, "radius": 0.5 * mm});
            skCircle(sketch, "E6.26.6.0", {"center": v(25.4, 1.27) * mm, "radius": 0.5 * mm});
            skCircle(sketch, "E6.26.7.0", {"center": v(25.4, 3.8) * mm, "radius": 0.5 * mm});
            skCircle(sketch, "E6.26.8.0", {"center": v(25.4, 6.35) * mm, "radius": 0.5 * mm});
            skCircle(sketch, "E6.26.9.0", {"center": v(25.4, 8.89) * mm, "radius": 0.5 * mm});
            skCircle(sketch, "E6.26.10.0", {"center": v(25.4, 11.43) * mm, "radius": 0.5 * mm});
            skCircle(sketch, "E6.26.11.0", {"center": v(25.4, 13.97) * mm, "radius": 0.5 * mm});
            skCircle(sketch, "E6.27.0.0", {"center": v(27.94, -13.97) * mm, "radius": 0.5 * mm});
            skCircle(sketch, "E6.27.1.0", {"center": v(27.94, -11.43) * mm, "radius": 0.5 * mm});
            skCircle(sketch, "E6.27.2.0", {"center": v(27.94, -8.9) * mm, "radius": 0.5 * mm});
            skCircle(sketch, "E6.27.3.0", {"center": v(27.94, -6.35) * mm, "radius": 0.5 * mm});
            skCircle(sketch, "E6.27.4.0", {"center": v(27.94, -3.81) * mm, "radius": 0.5 * mm});
            skCircle(sketch, "E6.27.5.0", {"center": v(27.94, -1.27) * mm, "radius": 0.5 * mm});
            skCircle(sketch, "E6.27.6.0", {"center": v(27.94, 1.27) * mm, "radius": 0.5 * mm});
            skCircle(sketch, "E6.27.7.0", {"center": v(27.94, 3.8) * mm, "radius": 0.5 * mm});
            skCircle(sketch, "E6.27.8.0", {"center": v(27.94, 6.35) * mm, "radius": 0.5 * mm});
            skCircle(sketch, "E6.27.9.0", {"center": v(27.94, 8.89) * mm, "radius": 0.5 * mm});
            skCircle(sketch, "E6.27.10.0", {"center": v(27.94, 11.43) * mm, "radius": 0.5 * mm});
            skCircle(sketch, "E6.27.11.0", {"center": v(27.94, 13.97) * mm, "radius": 0.5 * mm});
            skCircle(sketch, "E6.28.0.0", {"center": v(30.48, -13.97) * mm, "radius": 0.5 * mm});
            skCircle(sketch, "E6.28.1.0", {"center": v(30.48, -11.43) * mm, "radius": 0.5 * mm});
            skCircle(sketch, "E6.28.2.0", {"center": v(30.48, -8.9) * mm, "radius": 0.5 * mm});
            skCircle(sketch, "E6.28.3.0", {"center": v(30.48, -6.35) * mm, "radius": 0.5 * mm});
            skCircle(sketch, "E6.28.4.0", {"center": v(30.48, -3.81) * mm, "radius": 0.5 * mm});
            skCircle(sketch, "E6.28.5.0", {"center": v(30.48, -1.27) * mm, "radius": 0.5 * mm});
            skCircle(sketch, "E6.28.6.0", {"center": v(30.48, 1.27) * mm, "radius": 0.5 * mm});
            skCircle(sketch, "E6.28.7.0", {"center": v(30.48, 3.8) * mm, "radius": 0.5 * mm});
            skCircle(sketch, "E6.28.8.0", {"center": v(30.48, 6.35) * mm, "radius": 0.5 * mm});
            skCircle(sketch, "E6.28.9.0", {"center": v(30.48, 8.89) * mm, "radius": 0.5 * mm});
            skCircle(sketch, "E6.28.10.0", {"center": v(30.48, 11.43) * mm, "radius": 0.5 * mm});
            skCircle(sketch, "E6.28.11.0", {"center": v(30.48, 13.97) * mm, "radius": 0.5 * mm});
            skCircle(sketch, "E6.29.0.0", {"center": v(33.02, -13.97) * mm, "radius": 0.5 * mm});
            skCircle(sketch, "E6.29.1.0", {"center": v(33.02, -11.43) * mm, "radius": 0.5 * mm});
            skCircle(sketch, "E6.29.2.0", {"center": v(33.02, -8.9) * mm, "radius": 0.5 * mm});
            skCircle(sketch, "E6.29.3.0", {"center": v(33.02, -6.35) * mm, "radius": 0.5 * mm});
            skCircle(sketch, "E6.29.4.0", {"center": v(33.02, -3.81) * mm, "radius": 0.5 * mm});
            skCircle(sketch, "E6.29.5.0", {"center": v(33.02, -1.27) * mm, "radius": 0.5 * mm});
            skCircle(sketch, "E6.29.6.0", {"center": v(33.02, 1.27) * mm, "radius": 0.5 * mm});
            skCircle(sketch, "E6.29.7.0", {"center": v(33.02, 3.8) * mm, "radius": 0.5 * mm});
            skCircle(sketch, "E6.29.8.0", {"center": v(33.02, 6.35) * mm, "radius": 0.5 * mm});
            skCircle(sketch, "E6.29.9.0", {"center": v(33.02, 8.89) * mm, "radius": 0.5 * mm});
            skCircle(sketch, "E6.29.10.0", {"center": v(33.02, 11.43) * mm, "radius": 0.5 * mm});
            skCircle(sketch, "E6.29.11.0", {"center": v(33.02, 13.97) * mm, "radius": 0.5 * mm});
            skCircle(sketch, "E6.30.0.0", {"center": v(35.56, -13.97) * mm, "radius": 0.5 * mm});
            skCircle(sketch, "E6.30.1.0", {"center": v(35.56, -11.43) * mm, "radius": 0.5 * mm});
            skCircle(sketch, "E6.30.2.0", {"center": v(35.56, -8.9) * mm, "radius": 0.5 * mm});
            skCircle(sketch, "E6.30.3.0", {"center": v(35.56, -6.35) * mm, "radius": 0.5 * mm});
            skCircle(sketch, "E6.30.4.0", {"center": v(35.56, -3.81) * mm, "radius": 0.5 * mm});
            skCircle(sketch, "E6.30.5.0", {"center": v(35.56, -1.27) * mm, "radius": 0.5 * mm});
            skCircle(sketch, "E6.30.6.0", {"center": v(35.56, 1.27) * mm, "radius": 0.5 * mm});
            skCircle(sketch, "E6.30.7.0", {"center": v(35.56, 3.8) * mm, "radius": 0.5 * mm});
            skCircle(sketch, "E6.30.8.0", {"center": v(35.56, 6.35) * mm, "radius": 0.5 * mm});
            skCircle(sketch, "E6.30.9.0", {"center": v(35.56, 8.89) * mm, "radius": 0.5 * mm});
            skCircle(sketch, "E6.30.10.0", {"center": v(35.56, 11.43) * mm, "radius": 0.5 * mm});
            skCircle(sketch, "E6.30.11.0", {"center": v(35.56, 13.97) * mm, "radius": 0.5 * mm});
            skCircle(sketch, "E6.31.0.0", {"center": v(38.1, -13.97) * mm, "radius": 0.5 * mm});
            skCircle(sketch, "E6.31.1.0", {"center": v(38.1, -11.43) * mm, "radius": 0.5 * mm});
            skCircle(sketch, "E6.31.2.0", {"center": v(38.1, -8.9) * mm, "radius": 0.5 * mm});
            skCircle(sketch, "E6.31.3.0", {"center": v(38.1, -6.35) * mm, "radius": 0.5 * mm});
            skCircle(sketch, "E6.31.4.0", {"center": v(38.1, -3.81) * mm, "radius": 0.5 * mm});
            skCircle(sketch, "E6.31.5.0", {"center": v(38.1, -1.27) * mm, "radius": 0.5 * mm});
            skCircle(sketch, "E6.31.6.0", {"center": v(38.1, 1.27) * mm, "radius": 0.5 * mm});
            skCircle(sketch, "E6.31.7.0", {"center": v(38.1, 3.8) * mm, "radius": 0.5 * mm});
            skCircle(sketch, "E6.31.8.0", {"center": v(38.1, 6.35) * mm, "radius": 0.5 * mm});
            skCircle(sketch, "E6.31.9.0", {"center": v(38.1, 8.89) * mm, "radius": 0.5 * mm});
            skCircle(sketch, "E6.31.10.0", {"center": v(38.1, 11.43) * mm, "radius": 0.5 * mm});
            skCircle(sketch, "E6.31.11.0", {"center": v(38.1, 13.97) * mm, "radius": 0.5 * mm});
            skCircle(sketch, "E6.32.0.0", {"center": v(40.64, -13.97) * mm, "radius": 0.5 * mm});
            skCircle(sketch, "E6.32.1.0", {"center": v(40.64, -11.43) * mm, "radius": 0.5 * mm});
            skCircle(sketch, "E6.32.2.0", {"center": v(40.64, -8.9) * mm, "radius": 0.5 * mm});
            skCircle(sketch, "E6.32.3.0", {"center": v(40.64, -6.35) * mm, "radius": 0.5 * mm});
            skCircle(sketch, "E6.32.4.0", {"center": v(40.64, -3.81) * mm, "radius": 0.5 * mm});
            skCircle(sketch, "E6.32.5.0", {"center": v(40.64, -1.27) * mm, "radius": 0.5 * mm});
            skCircle(sketch, "E6.32.6.0", {"center": v(40.64, 1.27) * mm, "radius": 0.5 * mm});
            skCircle(sketch, "E6.32.7.0", {"center": v(40.64, 3.8) * mm, "radius": 0.5 * mm});
            skCircle(sketch, "E6.32.8.0", {"center": v(40.64, 6.35) * mm, "radius": 0.5 * mm});
            skCircle(sketch, "E6.32.9.0", {"center": v(40.64, 8.89) * mm, "radius": 0.5 * mm});
            skCircle(sketch, "E6.32.10.0", {"center": v(40.64, 11.43) * mm, "radius": 0.5 * mm});
            skCircle(sketch, "E6.32.11.0", {"center": v(40.64, 13.97) * mm, "radius": 0.5 * mm});
            skLineSegment(sketch, "E6.direction1", {"start": v(-40.64, -13.97) * mm, "end": v(-38.1, -13.97) * mm, "construction": true});
            skLineSegment(sketch, "E6.direction2", {"start": v(-40.64, -13.97) * mm, "end": v(-40.64, -11.43) * mm, "construction": true});
            skCircle(sketch, "E7", {"center": v(45.72, -6.35) * mm, "radius": 0.5 * mm});
            skCircle(sketch, "E8.0.1.0", {"center": v(45.72, -3.8) * mm, "radius": 0.5 * mm});
            skCircle(sketch, "E8.0.2.0", {"center": v(45.72, -1.27) * mm, "radius": 0.5 * mm});
            skCircle(sketch, "E8.0.3.0", {"center": v(45.72, 1.27) * mm, "radius": 0.5 * mm});
            skCircle(sketch, "E8.0.4.0", {"center": v(45.72, 3.81) * mm, "radius": 0.5 * mm});
            skCircle(sketch, "E8.0.5.0", {"center": v(45.72, 6.35) * mm, "radius": 0.5 * mm});
            skCircle(sketch, "E8.1.0.0", {"center": v(48.26, -6.35) * mm, "radius": 0.5 * mm});
            skCircle(sketch, "E8.1.1.0", {"center": v(48.26, -3.8) * mm, "radius": 0.5 * mm});
            skCircle(sketch, "E8.1.2.0", {"center": v(48.26, -1.27) * mm, "radius": 0.5 * mm});
            skCircle(sketch, "E8.1.3.0", {"center": v(48.26, 1.27) * mm, "radius": 0.5 * mm});
            skCircle(sketch, "E8.1.4.0", {"center": v(48.26, 3.81) * mm, "radius": 0.5 * mm});
            skCircle(sketch, "E8.1.5.0", {"center": v(48.26, 6.35) * mm, "radius": 0.5 * mm});
            skLineSegment(sketch, "E8.direction1", {"start": v(45.72, -6.35) * mm, "end": v(48.26, -6.35) * mm, "construction": true});
            skLineSegment(sketch, "E8.direction2", {"start": v(45.72, -6.35) * mm, "end": v(45.72, -3.8) * mm, "construction": true});
            skSolve(sketch);
        }
        {
            var Q0;
            Q0=makeQuery(id+"F0.imprint","IMPRINT",FACE,{"disambiguationData":[TD([[makeQuery(id+"F0.imprint","IMPRINT",EDGE,{"derivedFrom":sQuery(id+"F0.wireOp",EDGE,"E0.bottom")}),-1.0]])]});
            extrude(context, id + "F1", {"entities" : qUnion([Q0]), "depth" : 1.6 * mm, "offsetDistance" : 25 * mm});
        }
    });
